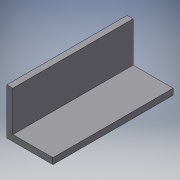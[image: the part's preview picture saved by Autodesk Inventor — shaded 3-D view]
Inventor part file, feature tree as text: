
AUTODESK INVENTOR PART (.ipt)
format: ipt  version: 2019 (Build 230136000, 136)  size: 99,328 bytes
history: native  units: mm
features: extrude x2, sketch x2
ambient origin geometry x8: Origin, YZ Plane, XZ Plane, XY Plane, X Axis, Y Axis, Z Axis, Center Point
bodies: Solid1 (feature_tree)
feature tree (4):
  extrude  "Extrusion1"  Depth=60.0mm
  extrude  "Extrusion2"  Depth=3.0mm
  sketch  "Sketch1"  dims[d0=23.0mm d1=60.0mm]
  sketch  "Sketch2"  dims[d2=3.0mm d3=0.0mm d4=3.0mm d5=20.0mm d6=0.0mm]
